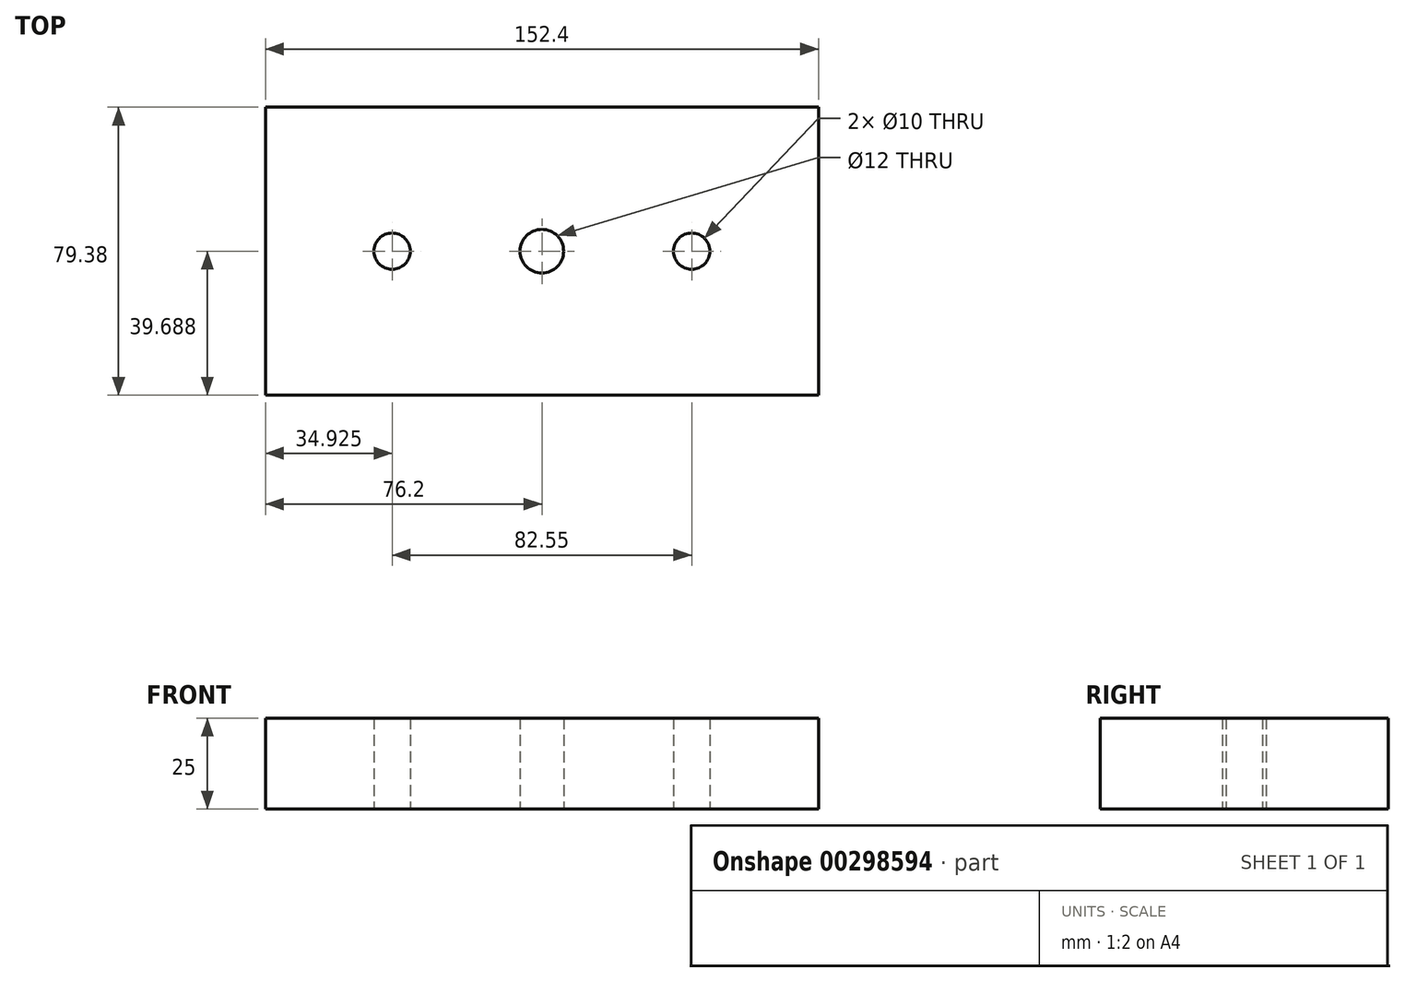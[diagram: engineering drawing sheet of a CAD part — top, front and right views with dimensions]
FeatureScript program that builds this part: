
annotation { "Feature Type Name" : "Feature", "Feature Type Description" : "" }
export const myFeature = defineFeature(function(context is Context, id is Id, definition is map)
    precondition{}
    {
        {
            var Q0;
            Q0=qCreatedBy(makeId("Top.planeOp"),FACE);
            var sketch = newSketch(context, id + "F0", { "sketchPlane" : qUnion([Q0])});
            skLineSegment(sketch, "E0.bottom", {"start": v(0, 0) * mm, "end": v(152.4, 0) * mm});
            skLineSegment(sketch, "E0.top", {"start": v(0, 79.38) * mm, "end": v(152.4, 79.38) * mm});
            skLineSegment(sketch, "E0.left", {"start": v(0, 0) * mm, "end": v(0, 79.38) * mm});
            skLineSegment(sketch, "E0.right", {"start": v(152.4, 0) * mm, "end": v(152.4, 79.38) * mm});
            skLineSegment(sketch, "E1", {"start": v(0, 39.69) * mm, "end": v(152.4, 39.69) * mm, "construction": true});
            skCircle(sketch, "E2", {"center": v(117.47, 39.69) * mm, "radius": 5 * mm});
            skCircle(sketch, "E3", {"center": v(34.92, 39.69) * mm, "radius": 5 * mm});
            skCircle(sketch, "E4", {"center": v(76.2, 39.69) * mm, "radius": 6 * mm});
            skSolve(sketch);
        }
        {
            var Q0;
            Q0 = qSketchRegion(id + "F0", true);
            extrude(context, id + "F1", {"entities" : qUnion([Q0]), "depth" : 25 * mm});
        }
    });
